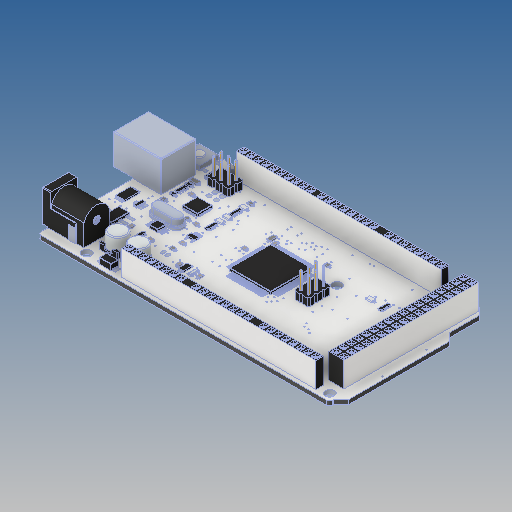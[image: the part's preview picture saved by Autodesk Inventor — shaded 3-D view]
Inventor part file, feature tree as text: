
AUTODESK INVENTOR PART (.ipt)
format: ipt  version: 2020 (Build 240168000, 168)  size: 2,687,488 bytes
history: native  units: mm
features: other x1, fillet x1
ambient origin geometry x8: Origin, YZ Plane, XZ Plane, XY Plane, X Axis, Y Axis, Z Axis, Center Point
bodies: Body1 (feature_tree)
feature tree (2):
  other  "Твердое тело1"
  fillet  "Fillet13"  [1 undecoded]
note: 1 required parameter value undecoded (feature->parameter linkage not recoverable at this tier; creation-order binding heuristic only, values carry confidence <= 0.55)
